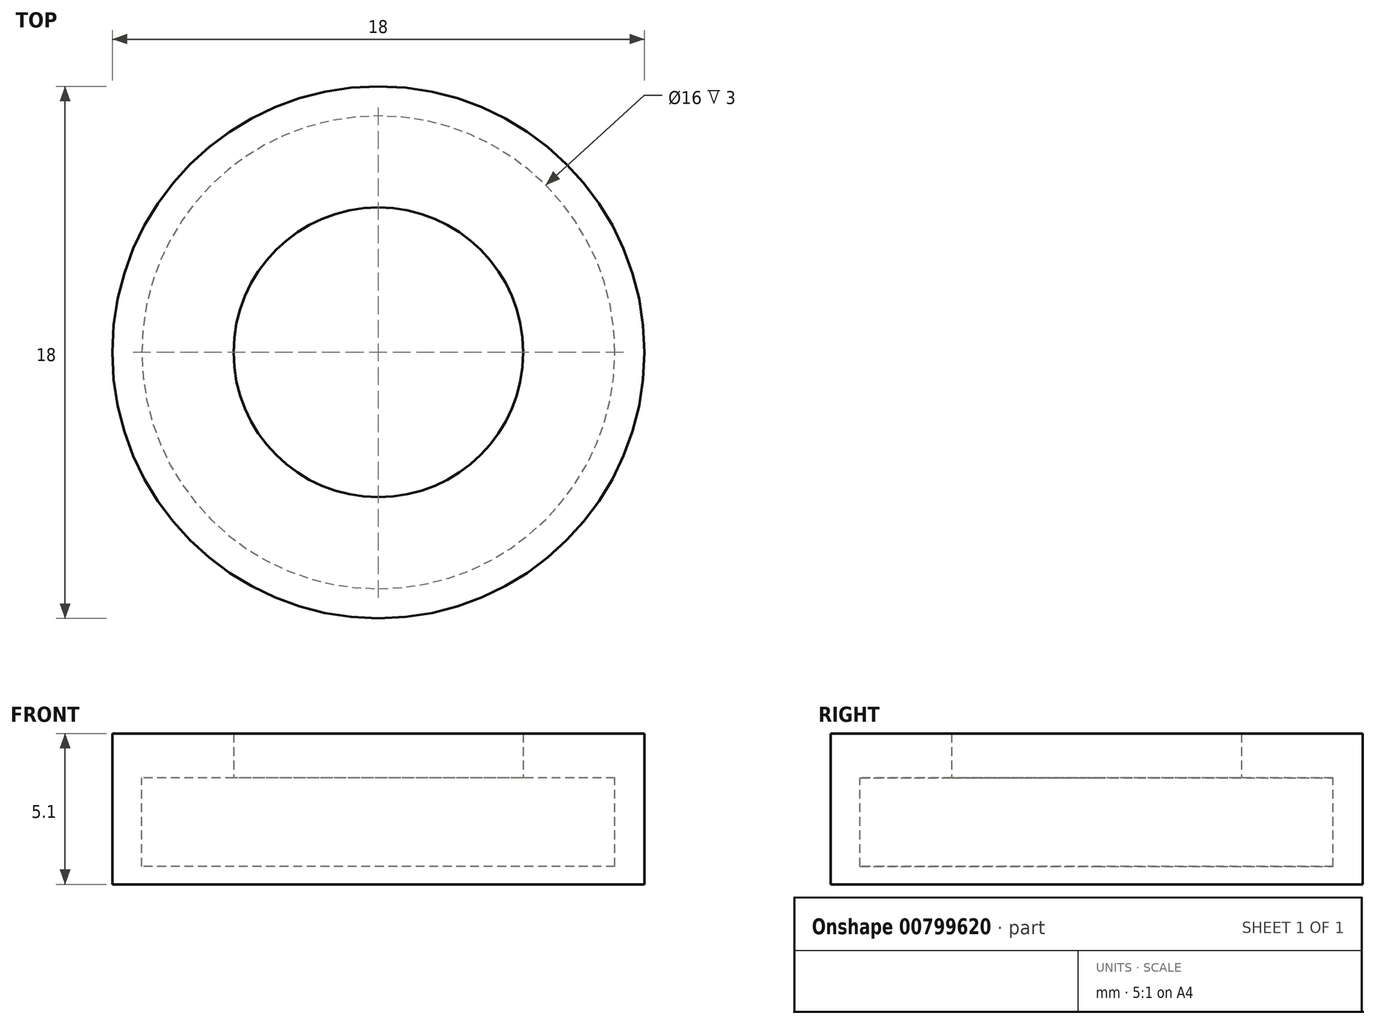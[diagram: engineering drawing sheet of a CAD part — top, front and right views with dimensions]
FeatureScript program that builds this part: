
annotation { "Feature Type Name" : "Feature", "Feature Type Description" : "" }
export const myFeature = defineFeature(function(context is Context, id is Id, definition is map)
    precondition{}
    {
        {
            var Q0;
            Q0=qCreatedBy(makeId("Top.planeOp"),FACE);
            var sketch = newSketch(context, id + "F0", { "sketchPlane" : qUnion([Q0])});
            skCircle(sketch, "E0", {"center": v(0, 0) * mm, "radius": 9 * mm});
            skSolve(sketch);
        }
        {
            var Q0;
            Q0 = qSketchRegion(id + "F0", true);
            extrude(context, id + "F1", {"entities" : qUnion([Q0]), "depth" : 3.6 * mm, "offsetDistance" : 25 * mm});
        }
        {
            var Q0;
            Q0=makeQuery(id+"F1.opExtrude","CAP_FACE",FACE,{"disambiguationData":[OSD([sQuery(id+"F0.wireOp",EDGE,"E0")])],"isStart":false});
            var sketch = newSketch(context, id + "F2", { "sketchPlane" : qUnion([Q0])});
            skCircle(sketch, "E1.0.0", {"center": v(0, 0) * mm, "radius": 9 * mm});
            skCircle(sketch, "E2", {"center": v(0, 0) * mm, "radius": 8 * mm});
            skSolve(sketch);
        }
        {
            var Q0;
            Q0=makeQuery(id+"F2.imprint","IMPRINT",FACE,{"disambiguationData":[TD([[makeQuery(id+"F2.imprint","IMPRINT",EDGE,{"derivedFrom":sQuery(id+"F2.wireOp",EDGE,"E2")}),1.0]])]});
            extrude(context, id + "F3", {"entities" : qUnion([Q0]), "operationType" : NewBodyOperationType.REMOVE, "oppositeDirection" : true, "depth" : 3 * mm, "offsetDistance" : 25 * mm});
        }
        {
            var Q0;
            Q0=makeQuery(id+"F1.opExtrude","CAP_FACE",FACE,{"disambiguationData":[OSD([sQuery(id+"F0.wireOp",EDGE,"E0")])],"isStart":false});
            var sketch = newSketch(context, id + "F4", { "sketchPlane" : qUnion([Q0])});
            skCircle(sketch, "E3.0", {"center": v(0, 0) * mm, "radius": 9 * mm});
            skCircle(sketch, "E4", {"center": v(0, 0) * mm, "radius": 4.9 * mm});
            skSolve(sketch);
        }
        {
            var Q0;
            Q0 = qSketchRegion(id + "F4", true);
            extrude(context, id + "F5", {"entities" : qUnion([Q0]), "operationType" : NewBodyOperationType.ADD, "depth" : 1.5 * mm, "offsetDistance" : 25 * mm});
        }
    });
